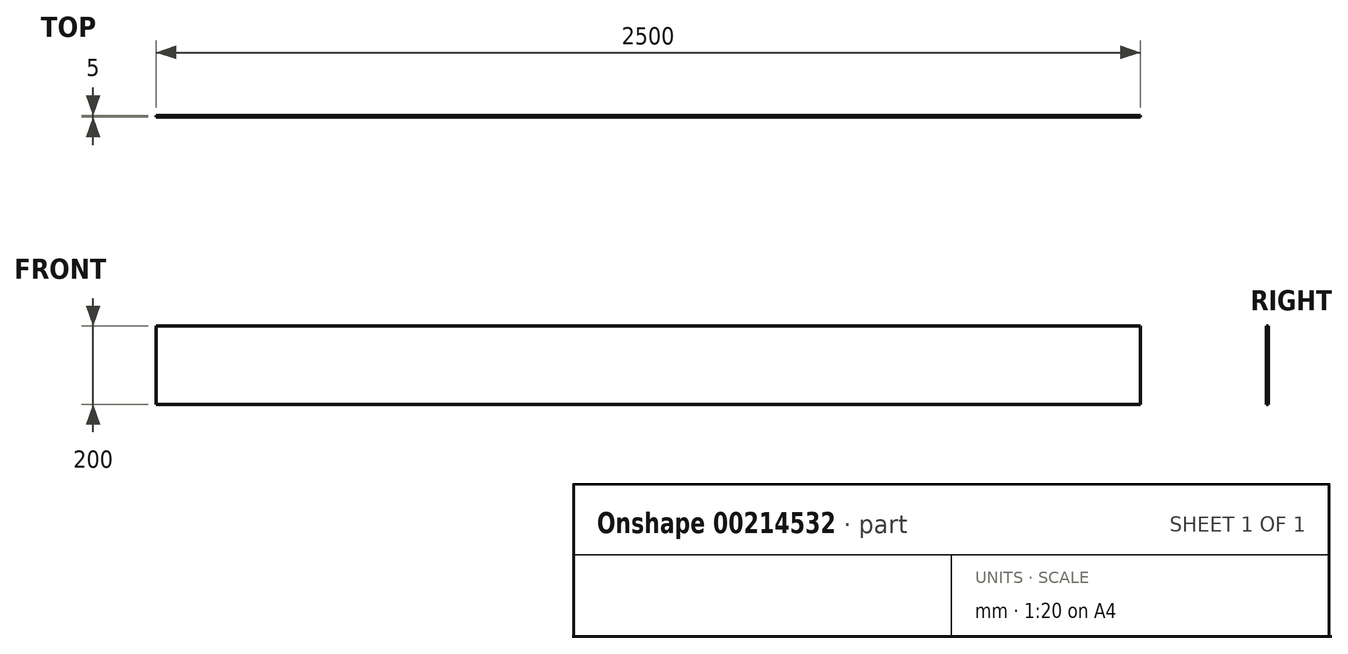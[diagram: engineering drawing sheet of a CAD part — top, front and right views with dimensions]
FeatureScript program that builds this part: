
annotation { "Feature Type Name" : "Feature", "Feature Type Description" : "" }
export const myFeature = defineFeature(function(context is Context, id is Id, definition is map)
    precondition{}
    {
        {
            var Q0;
            Q0=qCreatedBy(makeId("Front.planeOp"),FACE);
            var sketch = newSketch(context, id + "F0", { "sketchPlane" : qUnion([Q0])});
            skLineSegment(sketch, "E0.bottom", {"start": v(-1250, 100) * mm, "end": v(1250, 100) * mm});
            skLineSegment(sketch, "E0.top", {"start": v(-1250, -100) * mm, "end": v(1250, -100) * mm});
            skLineSegment(sketch, "E0.left", {"start": v(-1250, 100) * mm, "end": v(-1250, -100) * mm});
            skLineSegment(sketch, "E0.right", {"start": v(1250, 100) * mm, "end": v(1250, -100) * mm});
            skSolve(sketch);
        }
        {
            var Q0;
            Q0 = qSketchRegion(id + "F0", true);
            extrude(context, id + "F1", {"entities" : qUnion([Q0]), "depth" : 5 * mm});
        }
    });
